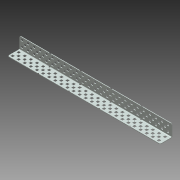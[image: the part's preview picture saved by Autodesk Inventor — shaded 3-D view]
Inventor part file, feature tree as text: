
AUTODESK INVENTOR PART (.ipt)
format: ipt  version: 2013 (Build 170138000, 138)  size: 1,484,288 bytes
history: native  units: mm (DEFAULTED — no unit token found)
features: other x154, extrude x148, sketch x10, sheet_metal_op x4, pattern_linear x4
ambient origin geometry x8: Origin, YZ Plane, XZ Plane, XY Plane, X Axis, Y Axis, Z Axis, Center Point
bodies: Solid1 (feature_tree)
feature tree (320):
  sheet_metal_op  "Face2"
  sheet_metal_op  "Flange8"
  pattern_linear  "Rectangular Pattern1"  Count1=24 Spacing1=12.7mm
  pattern_linear  "Rectangular Pattern2"  Spacing1=4.572mm  [1 undecoded]
  pattern_linear  "Rectangular Pattern3"  Spacing1=9.017mm  [1 undecoded]
  pattern_linear  "Rectangular Pattern4"  Spacing1=9.144mm  [1 undecoded]
  sketch  "Sketch1"  dims[d20=2.794mm]
  other  "Plate9"
  sketch  "Sketch14"  dims[d22=2.921mm]
  other  "Plate10"
  sheet_metal_op  "Bend8"
  sheet_metal_op  "Corner1"
  sketch  "Sketch15"  dims[d23=22.86mm]
  sketch  "Sketch16"  dims[d24=4.572mm]
  sketch  "Sketch17"  dims[d25=8.128mm]
  sketch  "Sketch18"  dims[d26=4.572mm]
  sketch  "Sketch19"  dims[d27=1.27mm]
  other  "Srf1"
  other  "Srf2"
  other  "Srf3"
  other  "Srf4"
  other  "Srf5"
  other  "Srf6"
  other  "Srf7"
  other  "Srf8"
  other  "Srf9"
  other  "Srf10"
  other  "Srf11"
  other  "Srf12"
  other  "Srf13"
  other  "Srf14"
  other  "Srf15"
  other  "Srf16"
  other  "Srf17"
  other  "Srf18"
  other  "Srf19"
  other  "Srf20"
  other  "Srf21"
  other  "Srf22"
  other  "Srf23"
  other  "Srf24"
  other  "Srf25"
  other  "Srf26"
  other  "Srf27"
  other  "Srf28"
  other  "Srf29"
  other  "Srf30"
  other  "Srf31"
  other  "Srf32"
  other  "Srf33"
  other  "Srf34"
  other  "Srf35"
  other  "Srf36"
  other  "Srf37"
  other  "Srf38"
  other  "Srf39"
  other  "Srf40"
  other  "Srf41"
  other  "Srf42"
  other  "Srf43"
  other  "Srf44"
  other  "Srf45"
  other  "Srf46"
  other  "Srf47"
  other  "Srf48"
  other  "Srf49"
  other  "Srf50"
  sketch  "Sketch20"  dims[d125=317.5mm]
  other  "Srf51"
  other  "Srf52"
  other  "Srf53"
  other  "Srf54"
  other  "Srf55"
  other  "Srf56"
  other  "Srf57"
  other  "Srf58"
  other  "Srf59"
  other  "Srf60"
  other  "Srf61"
  other  "Srf62"
  other  "Srf63"
  other  "Srf64"
  other  "Srf65"
  other  "Srf66"
  other  "Srf67"
  other  "Srf68"
  other  "Srf69"
  other  "Srf70"
  other  "Srf71"
  other  "Srf72"
  other  "Srf73"
  other  "Srf74"
  sketch  "Sketch21"  dims[d126=4.572mm]
  other  "Srf75"
  other  "Srf76"
  other  "Srf77"
  other  "Srf78"
  other  "Srf79"
  other  "Srf80"
  other  "Srf81"
  other  "Srf82"
  other  "Srf83"
  other  "Srf84"
  other  "Srf85"
  other  "Srf86"
  other  "Srf87"
  other  "Srf88"
  other  "Srf89"
  other  "Srf90"
  other  "Srf91"
  other  "Srf92"
  other  "Srf93"
  other  "Srf94"
  other  "Srf95"
  other  "Srf96"
  other  "Srf97"
  other  "Srf98"
  other  "Srf99"
  other  "Srf100"
  other  "Srf101"
  other  "Srf102"
  other  "Srf103"
  other  "Srf104"
  other  "Srf105"
  other  "Srf106"
  other  "Srf107"
  other  "Srf108"
  other  "Srf109"
  other  "Srf110"
  other  "Srf111"
  other  "Srf112"
  other  "Srf113"
  other  "Srf114"
  other  "Srf115"
  other  "Srf116"
  other  "Srf117"
  other  "Srf118"
  other  "Srf119"
  other  "Srf120"
  other  "Srf121"
  other  "Srf122"
  other  "Srf123"
  other  "Srf124"
  sketch  "Sketch22"  dims[d127=4.572mm d128=4.572mm d129=9.017mm d130=9.144mm d133=15.494mm d134=4.572mm d136=1.27mm d138=1.27mm d139=0.635mm d140=2.54mm d141=1.27mm d142=25.4mm d143=90.0deg d144=1.27mm d145=5.08mm d146=1.27mm d147=1.27mm d148=2.921mm d149=4.572mm d150=8.128mm d151=4.572mm d152=2.794mm d153=4.572mm d154=9.144mm d155=4.572mm d156=4.572mm d157=15.494mm d158=4.572mm d159=9.017mm d160=240.0mm d162=12.7mm d163=10.0mm d165=25.4mm d167=1.27mm d168=0.0mm d169=1.905mm d170=60.0mm d172=63.5mm d173=10.0mm d175=25.4mm d177=1.27mm d178=0.0mm d179=1.905mm d180=60.0mm d182=63.5mm d183=10.0mm d185=25.4mm d187=1.27mm d188=0.0mm d189=1.1176mm d190=1.905mm d191=40.0mm d193=63.5mm d194=10.0mm d196=25.4mm d198=1.27mm d199=0.0mm d200=25.4mm d201=0.0mm d202=250.0mm d204=12.7mm d205=20.0mm d207=12.7mm d208=25.4mm d209=0.0mm d210=240.0mm d212=12.7mm d213=0.0mm d214=0.0mm d215=0.0mm d216=0.0mm d217=0.0mm d218=0.0mm d219=0.0mm d220=0.0mm d221=0.0mm d222=0.0mm d223=0.0mm d224=0.0mm d225=0.0mm d226=0.0mm d227=0.0mm d228=0.0mm d229=0.0mm d230=0.0mm d231=0.0mm d232=0.0mm d233=0.0mm d234=0.0mm d235=0.0mm d236=0.0mm d237=0.0mm d238=0.0mm d239=0.0mm d240=0.0mm d241=0.0mm d242=0.0mm d243=0.0mm d244=0.0mm d245=0.0mm d246=0.0mm d247=0.0mm d248=0.0mm d249=0.0mm d250=0.0mm d251=0.0mm d252=0.0mm d253=0.0mm d254=0.0mm d255=0.0mm d256=0.0mm d257=0.0mm d258=0.0mm d259=0.0mm d260=0.0mm d261=0.0mm d262=0.0mm d263=0.0mm d264=0.0mm d265=0.0mm d266=0.0mm d267=0.0mm d268=0.0mm d269=0.0mm d270=0.0mm d271=0.0mm d272=0.0mm d273=0.0mm d274=0.0mm d275=0.0mm d276=0.0mm d277=0.0mm d278=0.0mm d279=0.0mm d280=0.0mm d281=0.0mm d282=0.0mm d283=0.0mm d284=0.0mm d285=0.0mm d286=0.0mm d287=0.0mm d288=0.0mm d289=0.0mm d290=0.0mm d291=0.0mm d292=0.0mm d293=0.0mm d294=0.0mm d295=0.0mm d296=0.0mm d297=0.0mm d298=0.0mm d299=0.0mm d300=0.0mm d301=0.0mm d302=0.0mm d303=0.0mm d304=0.0mm d305=0.0mm d306=0.0mm d307=0.0mm d308=0.0mm d309=0.0mm d310=0.0mm d311=0.0mm d312=0.0mm d313=0.0mm d314=0.0mm d315=0.0mm d316=0.0mm d317=0.0mm d318=0.0mm d319=0.0mm d320=0.0mm d321=0.0mm d322=0.0mm d323=0.0mm d324=0.0mm d325=0.0mm d326=0.0mm d327=0.0mm d328=0.0mm d329=0.0mm d330=0.0mm d331=0.0mm d332=0.0mm d333=0.0mm d334=0.0mm d335=0.0mm d336=0.0mm d337=0.0mm d338=0.0mm d339=0.0mm d340=0.0mm d341=0.0mm d342=0.0mm d343=0.0mm d344=0.0mm d345=0.0mm d346=0.0mm d347=0.0mm d348=0.0mm d349=0.0mm d350=0.0mm d351=0.0mm d352=0.0mm d353=0.0mm d354=0.0mm d355=0.0mm d356=0.0mm d357=0.0mm d358=0.0mm d359=0.0mm d360=25.4mm d361=0.0mm d362=250.0mm d364=12.7mm d365=20.0mm d367=12.7mm d368=25.4mm d369=0.0mm d370=240.0mm d372=12.7mm d373=0.0mm d374=0.0mm d375=0.0mm d376=0.0mm d377=0.0mm d378=0.0mm d379=0.0mm d380=0.0mm d381=0.0mm d382=0.0mm d383=0.0mm d384=0.0mm d385=0.0mm d386=0.0mm d387=0.0mm d388=0.0mm d389=0.0mm d390=0.0mm d391=0.0mm d392=0.0mm d393=0.0mm d394=0.0mm d395=0.0mm d396=0.0mm d397=0.0mm d398=0.0mm d399=0.0mm d400=0.0mm d401=0.0mm d402=0.0mm d403=0.0mm d404=0.0mm d405=0.0mm d406=0.0mm d407=0.0mm d408=0.0mm d409=0.0mm d410=0.0mm d411=0.0mm d412=0.0mm d413=0.0mm d414=0.0mm d415=0.0mm d416=0.0mm d417=0.0mm d418=0.0mm d419=0.0mm d420=0.0mm d421=0.0mm d422=0.0mm d423=0.0mm d424=0.0mm d425=0.0mm d426=0.0mm d427=0.0mm d428=0.0mm d429=0.0mm d430=0.0mm d431=0.0mm d432=0.0mm d433=0.0mm d434=0.0mm d435=0.0mm d436=0.0mm d437=0.0mm d438=0.0mm d439=0.0mm d440=0.0mm d441=0.0mm d442=0.0mm d443=0.0mm d444=0.0mm d445=0.0mm d446=0.0mm d447=0.0mm d448=0.0mm d449=0.0mm d450=0.0mm d451=0.0mm d452=0.0mm d453=0.0mm d454=0.0mm d455=0.0mm d456=0.0mm d457=0.0mm d458=0.0mm d459=0.0mm d460=0.0mm d461=0.0mm d462=0.0mm d463=0.0mm d464=0.0mm d465=0.0mm d466=0.0mm d467=0.0mm d468=0.0mm d469=0.0mm d470=0.0mm d471=0.0mm d472=0.0mm d473=0.0mm d474=0.0mm d475=0.0mm d476=0.0mm d477=0.0mm d478=0.0mm d479=0.0mm d480=0.0mm d481=0.0mm d482=0.0mm d483=0.0mm d484=0.0mm d485=0.0mm d486=0.0mm d487=0.0mm d488=0.0mm d489=0.0mm d490=0.0mm d491=0.0mm d492=0.0mm d493=0.0mm d494=0.0mm d495=0.0mm d496=0.0mm d497=0.0mm d498=0.0mm d499=0.0mm d500=0.0mm d501=0.0mm d502=0.0mm d503=0.0mm d504=0.0mm d505=0.0mm d506=0.0mm d507=0.0mm d508=0.0mm d509=0.0mm d510=0.0mm d511=0.0mm d512=0.0mm d513=0.0mm d514=0.0mm d515=0.0mm d516=0.0mm d517=0.0mm d518=0.0mm d519=0.0mm d520=0.0mm]
  other  "Srf125"
  other  "Srf126"
  other  "Srf127"
  other  "Srf128"
  other  "Srf129"
  other  "Srf130"
  other  "Srf131"
  other  "Srf132"
  other  "Srf133"
  other  "Srf134"
  other  "Srf135"
  other  "Srf136"
  other  "Srf137"
  other  "Srf138"
  other  "Srf139"
  other  "Srf140"
  other  "Srf141"
  other  "Srf142"
  other  "Srf143"
  other  "Srf144"
  other  "Srf145"
  other  "Srf146"
  other  "Srf147"
  other  "Srf148"
  other  "Cut4"
  other  "Cut5"
  other  "Cut6"
  other  "Cut7"
  extrude  "ExtrusionSrf1"  Depth=15.494mm
  extrude  "ExtrusionSrf51"  Depth=4.572mm
  extrude  "ExtrusionSrf75"  Depth=1.27mm
  extrude  "ExtrusionSrf125"  Depth=1.27mm
  extrude  "ExtrusionSrf2"  Depth=0.635mm
  extrude  "ExtrusionSrf3"  Depth=2.54mm
  extrude  "ExtrusionSrf4"  Depth=1.27mm
  extrude  "ExtrusionSrf5"  Depth=25.4mm TaperAngle=90.0deg
  extrude  "ExtrusionSrf6"  Depth=5.08mm
  extrude  "ExtrusionSrf7"  Depth=1.27mm
  extrude  "ExtrusionSrf8"  Depth=1.27mm
  extrude  "ExtrusionSrf9"  Depth=2.921mm
  extrude  "ExtrusionSrf10"  Depth=4.572mm
  extrude  "ExtrusionSrf11"  Depth=8.128mm
  extrude  "ExtrusionSrf12"  Depth=4.572mm
  extrude  "ExtrusionSrf13"  Depth=2.794mm
  extrude  "ExtrusionSrf14"  Depth=4.572mm
  extrude  "ExtrusionSrf15"  Depth=9.144mm
  extrude  "ExtrusionSrf16"  Depth=4.572mm
  extrude  "ExtrusionSrf17"  Depth=4.572mm
  extrude  "ExtrusionSrf18"  Depth=15.494mm
  extrude  "ExtrusionSrf19"  Depth=4.572mm
  extrude  "ExtrusionSrf20"  Depth=9.017mm
  extrude  "ExtrusionSrf21"  Depth=240.0mm
  extrude  "ExtrusionSrf22"  Depth=1.27mm
  extrude  "ExtrusionSrf23"  TaperAngle=0.0deg  [1 undecoded]
  extrude  "ExtrusionSrf24"  Depth=1.905mm
  extrude  "ExtrusionSrf25"  Depth=60.0mm
  extrude  "ExtrusionSrf26"  Depth=1.27mm
  extrude  "ExtrusionSrf27"  TaperAngle=0.0deg  [1 undecoded]
  extrude  "ExtrusionSrf28"  Depth=1.905mm
  extrude  "ExtrusionSrf29"  Depth=60.0mm
  extrude  "ExtrusionSrf30"  Depth=1.27mm
  extrude  "ExtrusionSrf31"  TaperAngle=0.0deg  [1 undecoded]
  extrude  "ExtrusionSrf32"  Depth=1.1176mm
  extrude  "ExtrusionSrf33"  Depth=1.905mm
  extrude  "ExtrusionSrf34"  Depth=40.0mm
  extrude  "ExtrusionSrf35"  Depth=1.27mm
  extrude  "ExtrusionSrf36"  TaperAngle=0.0deg  [1 undecoded]
  extrude  "ExtrusionSrf37"  Depth=25.4mm TaperAngle=0.0deg
  extrude  "ExtrusionSrf38"  Depth=250.0mm
  extrude  "ExtrusionSrf39"  Depth=20.0mm
  extrude  "ExtrusionSrf40"  Depth=25.4mm TaperAngle=0.0deg
  extrude  "ExtrusionSrf41"  Depth=240.0mm
  extrude  "ExtrusionSrf42"  TaperAngle=0.0deg  [1 undecoded]
  extrude  "ExtrusionSrf43"  TaperAngle=0.0deg  [1 undecoded]
  extrude  "ExtrusionSrf44"  TaperAngle=0.0deg  [1 undecoded]
  extrude  "ExtrusionSrf45"  TaperAngle=0.0deg  [1 undecoded]
  extrude  "ExtrusionSrf46"  TaperAngle=0.0deg  [1 undecoded]
  extrude  "ExtrusionSrf47"  TaperAngle=0.0deg  [1 undecoded]
  extrude  "ExtrusionSrf48"  TaperAngle=0.0deg  [1 undecoded]
  extrude  "ExtrusionSrf49"  TaperAngle=0.0deg  [1 undecoded]
  extrude  "ExtrusionSrf50"  TaperAngle=0.0deg  [1 undecoded]
  extrude  "ExtrusionSrf52"  TaperAngle=0.0deg  [1 undecoded]
  extrude  "ExtrusionSrf53"  TaperAngle=0.0deg  [1 undecoded]
  extrude  "ExtrusionSrf54"  TaperAngle=0.0deg  [1 undecoded]
  extrude  "ExtrusionSrf55"  TaperAngle=0.0deg  [1 undecoded]
  extrude  "ExtrusionSrf56"  TaperAngle=0.0deg  [1 undecoded]
  extrude  "ExtrusionSrf57"  TaperAngle=0.0deg  [1 undecoded]
  extrude  "ExtrusionSrf58"  TaperAngle=0.0deg  [1 undecoded]
  extrude  "ExtrusionSrf59"  TaperAngle=0.0deg  [1 undecoded]
  extrude  "ExtrusionSrf60"  TaperAngle=0.0deg  [1 undecoded]
  extrude  "ExtrusionSrf61"  TaperAngle=0.0deg  [1 undecoded]
  extrude  "ExtrusionSrf62"  TaperAngle=0.0deg  [1 undecoded]
  extrude  "ExtrusionSrf63"  TaperAngle=0.0deg  [1 undecoded]
  extrude  "ExtrusionSrf64"  TaperAngle=0.0deg  [1 undecoded]
  extrude  "ExtrusionSrf65"  TaperAngle=0.0deg  [1 undecoded]
  extrude  "ExtrusionSrf66"  TaperAngle=0.0deg  [1 undecoded]
  extrude  "ExtrusionSrf67"  TaperAngle=0.0deg  [1 undecoded]
  extrude  "ExtrusionSrf68"  TaperAngle=0.0deg  [1 undecoded]
  extrude  "ExtrusionSrf69"  TaperAngle=0.0deg  [1 undecoded]
  extrude  "ExtrusionSrf70"  TaperAngle=0.0deg  [1 undecoded]
  extrude  "ExtrusionSrf71"  TaperAngle=0.0deg  [1 undecoded]
  extrude  "ExtrusionSrf72"  TaperAngle=0.0deg  [1 undecoded]
  extrude  "ExtrusionSrf73"  TaperAngle=0.0deg  [1 undecoded]
  extrude  "ExtrusionSrf74"  TaperAngle=0.0deg  [1 undecoded]
  extrude  "ExtrusionSrf76"  TaperAngle=0.0deg  [1 undecoded]
  extrude  "ExtrusionSrf77"  TaperAngle=0.0deg  [1 undecoded]
  extrude  "ExtrusionSrf78"  TaperAngle=0.0deg  [1 undecoded]
  extrude  "ExtrusionSrf79"  TaperAngle=0.0deg  [1 undecoded]
  extrude  "ExtrusionSrf80"  TaperAngle=0.0deg  [1 undecoded]
  extrude  "ExtrusionSrf81"  TaperAngle=0.0deg  [1 undecoded]
  extrude  "ExtrusionSrf82"  TaperAngle=0.0deg  [1 undecoded]
  extrude  "ExtrusionSrf83"  TaperAngle=0.0deg  [1 undecoded]
  extrude  "ExtrusionSrf84"  TaperAngle=0.0deg  [1 undecoded]
  extrude  "ExtrusionSrf85"  TaperAngle=0.0deg  [1 undecoded]
  extrude  "ExtrusionSrf86"  TaperAngle=0.0deg  [1 undecoded]
  extrude  "ExtrusionSrf87"  TaperAngle=0.0deg  [1 undecoded]
  extrude  "ExtrusionSrf88"  TaperAngle=0.0deg  [1 undecoded]
  extrude  "ExtrusionSrf89"  TaperAngle=0.0deg  [1 undecoded]
  extrude  "ExtrusionSrf90"  TaperAngle=0.0deg  [1 undecoded]
  extrude  "ExtrusionSrf91"  TaperAngle=0.0deg  [1 undecoded]
  extrude  "ExtrusionSrf92"  TaperAngle=0.0deg  [1 undecoded]
  extrude  "ExtrusionSrf93"  TaperAngle=0.0deg  [1 undecoded]
  extrude  "ExtrusionSrf94"  TaperAngle=0.0deg  [1 undecoded]
  extrude  "ExtrusionSrf95"  TaperAngle=0.0deg  [1 undecoded]
  extrude  "ExtrusionSrf96"  TaperAngle=0.0deg  [1 undecoded]
  extrude  "ExtrusionSrf97"  TaperAngle=0.0deg  [1 undecoded]
  extrude  "ExtrusionSrf98"  TaperAngle=0.0deg  [1 undecoded]
  extrude  "ExtrusionSrf99"  TaperAngle=0.0deg  [1 undecoded]
  extrude  "ExtrusionSrf100"  TaperAngle=0.0deg  [1 undecoded]
  extrude  "ExtrusionSrf101"  TaperAngle=0.0deg  [1 undecoded]
  extrude  "ExtrusionSrf102"  TaperAngle=0.0deg  [1 undecoded]
  extrude  "ExtrusionSrf103"  TaperAngle=0.0deg  [1 undecoded]
  extrude  "ExtrusionSrf104"  TaperAngle=0.0deg  [1 undecoded]
  extrude  "ExtrusionSrf105"  TaperAngle=0.0deg  [1 undecoded]
  extrude  "ExtrusionSrf106"  TaperAngle=0.0deg  [1 undecoded]
  extrude  "ExtrusionSrf107"  TaperAngle=0.0deg  [1 undecoded]
  extrude  "ExtrusionSrf108"  TaperAngle=0.0deg  [1 undecoded]
  extrude  "ExtrusionSrf109"  TaperAngle=0.0deg  [1 undecoded]
  extrude  "ExtrusionSrf110"  TaperAngle=0.0deg  [1 undecoded]
  extrude  "ExtrusionSrf111"  TaperAngle=0.0deg  [1 undecoded]
  extrude  "ExtrusionSrf112"  TaperAngle=0.0deg  [1 undecoded]
  extrude  "ExtrusionSrf113"  TaperAngle=0.0deg  [1 undecoded]
  extrude  "ExtrusionSrf114"  TaperAngle=0.0deg  [1 undecoded]
  extrude  "ExtrusionSrf115"  TaperAngle=0.0deg  [1 undecoded]
  extrude  "ExtrusionSrf116"  TaperAngle=0.0deg  [1 undecoded]
  extrude  "ExtrusionSrf117"  TaperAngle=0.0deg  [1 undecoded]
  extrude  "ExtrusionSrf118"  TaperAngle=0.0deg  [1 undecoded]
  extrude  "ExtrusionSrf119"  TaperAngle=0.0deg  [1 undecoded]
  extrude  "ExtrusionSrf120"  TaperAngle=0.0deg  [1 undecoded]
  extrude  "ExtrusionSrf121"  TaperAngle=0.0deg  [1 undecoded]
  extrude  "ExtrusionSrf122"  TaperAngle=0.0deg  [1 undecoded]
  extrude  "ExtrusionSrf123"  TaperAngle=0.0deg  [1 undecoded]
  extrude  "ExtrusionSrf124"  TaperAngle=0.0deg  [1 undecoded]
  extrude  "ExtrusionSrf126"  TaperAngle=0.0deg  [1 undecoded]
  extrude  "ExtrusionSrf127"  TaperAngle=0.0deg  [1 undecoded]
  extrude  "ExtrusionSrf128"  TaperAngle=0.0deg  [1 undecoded]
  extrude  "ExtrusionSrf129"  TaperAngle=0.0deg  [1 undecoded]
  extrude  "ExtrusionSrf130"  TaperAngle=0.0deg  [1 undecoded]
  extrude  "ExtrusionSrf131"  TaperAngle=0.0deg  [1 undecoded]
  extrude  "ExtrusionSrf132"  TaperAngle=0.0deg  [1 undecoded]
  extrude  "ExtrusionSrf133"  TaperAngle=0.0deg  [1 undecoded]
  extrude  "ExtrusionSrf134"  TaperAngle=0.0deg  [1 undecoded]
  extrude  "ExtrusionSrf135"  TaperAngle=0.0deg  [1 undecoded]
  extrude  "ExtrusionSrf136"  TaperAngle=0.0deg  [1 undecoded]
  extrude  "ExtrusionSrf137"  TaperAngle=0.0deg  [1 undecoded]
  extrude  "ExtrusionSrf138"  TaperAngle=0.0deg  [1 undecoded]
  extrude  "ExtrusionSrf139"  TaperAngle=0.0deg  [1 undecoded]
  extrude  "ExtrusionSrf140"  TaperAngle=0.0deg  [1 undecoded]
  extrude  "ExtrusionSrf141"  TaperAngle=0.0deg  [1 undecoded]
  extrude  "ExtrusionSrf142"  TaperAngle=0.0deg  [1 undecoded]
  extrude  "ExtrusionSrf143"  TaperAngle=0.0deg  [1 undecoded]
  extrude  "ExtrusionSrf144"  TaperAngle=0.0deg  [1 undecoded]
  extrude  "ExtrusionSrf145"  TaperAngle=0.0deg  [1 undecoded]
  extrude  "ExtrusionSrf146"  TaperAngle=0.0deg  [1 undecoded]
  extrude  "ExtrusionSrf147"  TaperAngle=0.0deg  [1 undecoded]
  extrude  "ExtrusionSrf148"  TaperAngle=0.0deg  [1 undecoded]
note: 111 required parameter values undecoded (feature->parameter linkage not recoverable at this tier; creation-order binding heuristic only, values carry confidence <= 0.55)
